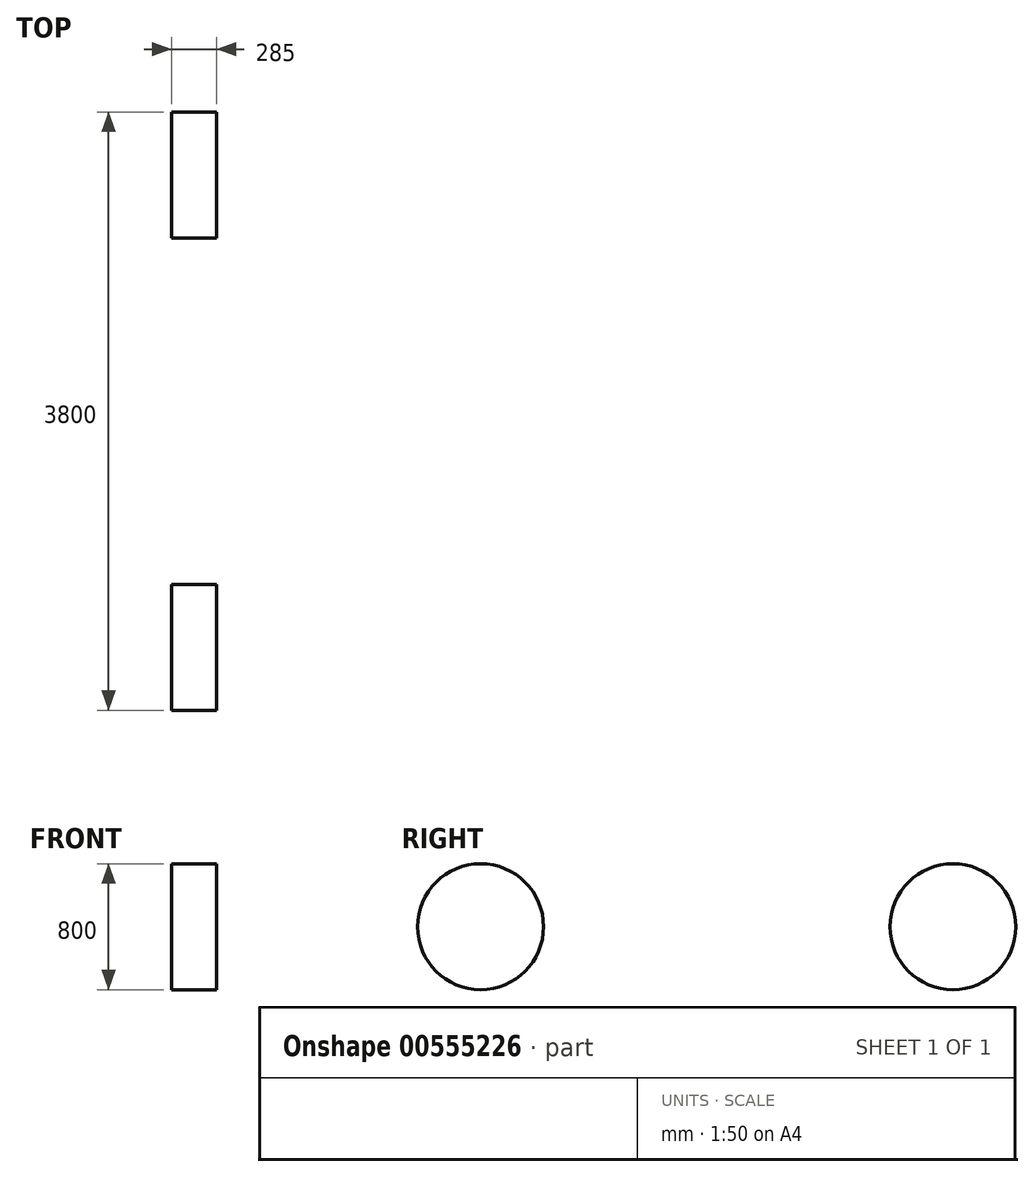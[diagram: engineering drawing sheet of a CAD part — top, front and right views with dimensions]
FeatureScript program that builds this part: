
annotation { "Feature Type Name" : "Feature", "Feature Type Description" : "" }
export const myFeature = defineFeature(function(context is Context, id is Id, definition is map)
    precondition{}
    {
        {
            var Q0;
            Q0=qCreatedBy(makeId("Right.planeOp"),FACE);
            var sketch = newSketch(context, id + "F0", { "sketchPlane" : qUnion([Q0])});
            skCircle(sketch, "E0", {"center": v(0, 400) * mm, "radius": 400 * mm});
            skCircle(sketch, "E1", {"center": v(3000, 400) * mm, "radius": 400 * mm});
            skPoint(sketch, "E2", {"position": v(3000, 0) * mm});
            skLineSegment(sketch, "E3", {"start": v(3383.82, 40) * mm, "end": v(3642.05, 907.5) * mm});
            skLineSegment(sketch, "E4", {"start": v(-304.94, 40) * mm, "end": v(-815.08, 153) * mm});
            skLineSegment(sketch, "E5", {"start": v(-815.08, 153) * mm, "end": v(-1050.54, 708.93) * mm});
            skLineSegment(sketch, "E6", {"start": v(-1050.54, 708.93) * mm, "end": v(277.15, 1049.03) * mm});
            skLineSegment(sketch, "E7", {"start": v(277.15, 1049.03) * mm, "end": v(983.51, 1526.48) * mm});
            skLineSegment(sketch, "E8", {"start": v(983.51, 1526.48) * mm, "end": v(3043.72, 1434.91) * mm});
            skLineSegment(sketch, "E9", {"start": v(3043.72, 1434.91) * mm, "end": v(3642.05, 907.5) * mm});
            skLineSegment(sketch, "E10", {"start": v(-304.94, 40) * mm, "end": v(3383.82, 40) * mm});
            skSolve(sketch);
        }
        {
            var Q0;
            Q0=qCreatedBy(makeId("Right.planeOp"),FACE);
            cPlane(context, id + "F1", {"entities" : qUnion([Q0]), "cplaneType" : CPlaneType.OFFSET, "offset" : 1300 * mm, "width" : 150 * mm, "height" : 150 * mm});
        }
        {
            var Q0;
            Q0=qCreatedBy(id+"F1.planeOp",FACE);
            var sketch = newSketch(context, id + "F2", { "sketchPlane" : qUnion([Q0])});
            skCircle(sketch, "E11.0", {"center": v(0, 400) * mm, "radius": 400 * mm});
            skCircle(sketch, "E12.0", {"center": v(3000, 400) * mm, "radius": 400 * mm});
            skSolve(sketch);
        }
        {
            var Q0;
            Q0 = qSketchRegion(id + "F2", true);
            extrude(context, id + "F3", {"entities" : qUnion([Q0]), "oppositeDirection" : true, "depth" : 285 * mm, "offsetDistance" : 25 * mm});
        }
    });
